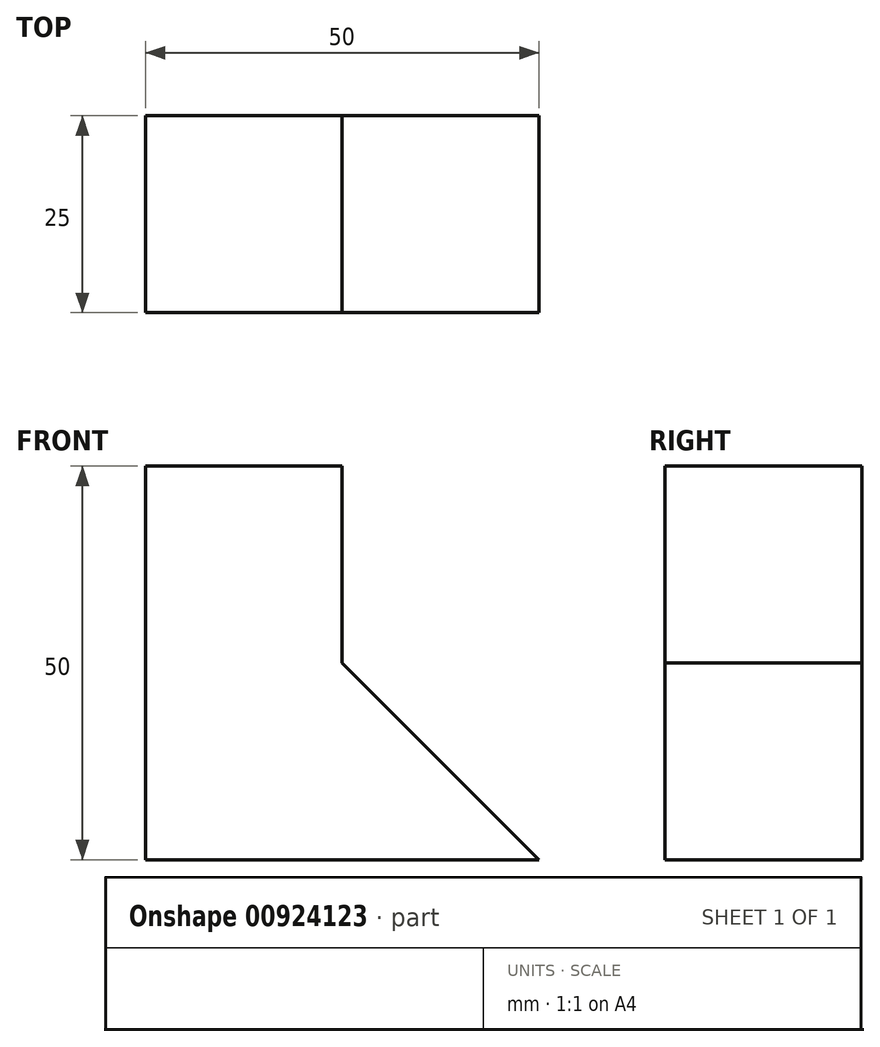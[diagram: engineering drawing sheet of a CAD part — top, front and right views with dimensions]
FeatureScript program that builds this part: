
annotation { "Feature Type Name" : "Feature", "Feature Type Description" : "" }
export const myFeature = defineFeature(function(context is Context, id is Id, definition is map)
    precondition{}
    {
        {
            var Q0;
            Q0=qCreatedBy(makeId("Front.planeOp"),FACE);
            var sketch = newSketch(context, id + "F0", { "sketchPlane" : qUnion([Q0])});
            skLineSegment(sketch, "E0.bottom", {"start": v(-25, 25) * mm, "end": v(25, 25) * mm});
            skLineSegment(sketch, "E0.top", {"start": v(-25, -25) * mm, "end": v(25, -25) * mm});
            skLineSegment(sketch, "E0.left", {"start": v(-25, 25) * mm, "end": v(-25, -25) * mm});
            skLineSegment(sketch, "E0.right", {"start": v(25, 25) * mm, "end": v(25, -25) * mm});
            skLineSegment(sketch, "E1", {"start": v(-25, 25) * mm, "end": v(25, -25) * mm});
            skPoint(sketch, "E2", {"position": v(0, 0) * mm});
            skPoint(sketch, "E3", {"position": v(-25, -25) * mm});
            skPoint(sketch, "E4", {"position": v(3.84, -15.03) * mm});
            skPoint(sketch, "E5.1.0", {"position": v(-35.22, -3.08) * mm});
            skPoint(sketch, "E5.1.3", {"position": v(3.15, -5.43) * mm});
            skPoint(sketch, "E5.2.0", {"position": v(-28.96, 20.28) * mm});
            skPoint(sketch, "E5.2.1", {"position": v(-14.14, -6.39) * mm});
            skPoint(sketch, "E5.2.3", {"position": v(-1.08, -6.18) * mm});
            skLineSegment(sketch, "E5.anchor1", {"start": v(0, 0) * mm, "end": v(-25, -25) * mm, "construction": true});
            skLineSegment(sketch, "E5.anchor2", {"start": v(0, 0) * mm, "end": v(-28.96, 20.28) * mm, "construction": true});
            skPoint(sketch, "E6.1.0.0", {"position": v(-13.6, -3.3) * mm});
            skPoint(sketch, "E6.1.0.1", {"position": v(-24.46, -21.91) * mm});
            skPoint(sketch, "E6.1.0.2", {"position": v(-34.68, 0) * mm});
            skPoint(sketch, "E6.1.0.3", {"position": v(-28.42, 23.37) * mm});
            skPoint(sketch, "E6.1.0.4", {"position": v(0.54, 3.09) * mm});
            skPoint(sketch, "E6.1.0.5", {"position": v(0.54, 3.09) * mm});
            skPoint(sketch, "E6.1.0.6", {"position": v(4.38, -11.94) * mm});
            skPoint(sketch, "E6.1.0.7", {"position": v(-0.54, -3.09) * mm});
            skPoint(sketch, "E6.1.0.8", {"position": v(-6.19, -10.9) * mm});
            skPoint(sketch, "E6.1.0.9", {"position": v(-0.54, -3.09) * mm});
            skPoint(sketch, "E6.1.0.10", {"position": v(0.54, 3.09) * mm});
            skPoint(sketch, "E6.2.0.0", {"position": v(-13.06, -0.21) * mm});
            skPoint(sketch, "E6.2.0.1", {"position": v(-23.92, -18.82) * mm});
            skPoint(sketch, "E6.2.0.2", {"position": v(-34.15, 3.1) * mm});
            skPoint(sketch, "E6.2.0.3", {"position": v(-27.89, 26.46) * mm});
            skPoint(sketch, "E6.2.0.5", {"position": v(1.08, 6.18) * mm});
            skPoint(sketch, "E6.2.0.8", {"position": v(-5.65, -7.8) * mm});
            skPoint(sketch, "E6.2.0.10", {"position": v(1.08, 6.18) * mm});
            skLineSegment(sketch, "E6.direction1", {"start": v(-14.14, -6.39) * mm, "end": v(-13.6, -3.3) * mm, "construction": true});
            skLineSegment(sketch, "E7", {"start": v(0, 43.73) * mm, "end": v(0, -11.95) * mm});
            skLineSegment(sketch, "E8", {"start": v(-13.3, 0) * mm, "end": v(42.38, 0) * mm});
            skSolve(sketch);
        }
        {
            var Q0;
            Q0=makeQuery(id+"F0.imprint","IMPRINT",FACE,{"disambiguationData":[TD([[makeQuery(id+"F0.imprint","IMPRINT",EDGE,{"derivedFrom":sQuery(id+"F0.wireOp",EDGE,"E0.top")}),1.0]])]});
            var Q1;
            Q1=makeQuery(id+"F0.imprint","IMPRINT",FACE,{"disambiguationData":[TD([[makeQuery(id+"F0.imprint","IMPRINT",EDGE,{"derivedFrom":sQuery(id+"F0.wireOp",EDGE,"E0.bottom")}),-1.0]])]});
            extrude(context, id + "F1", {"entities" : qUnion([Q0, Q1]), "oppositeDirection" : true, "depth" : 25 * mm, "offsetDistance" : 25 * mm});
        }
    });
